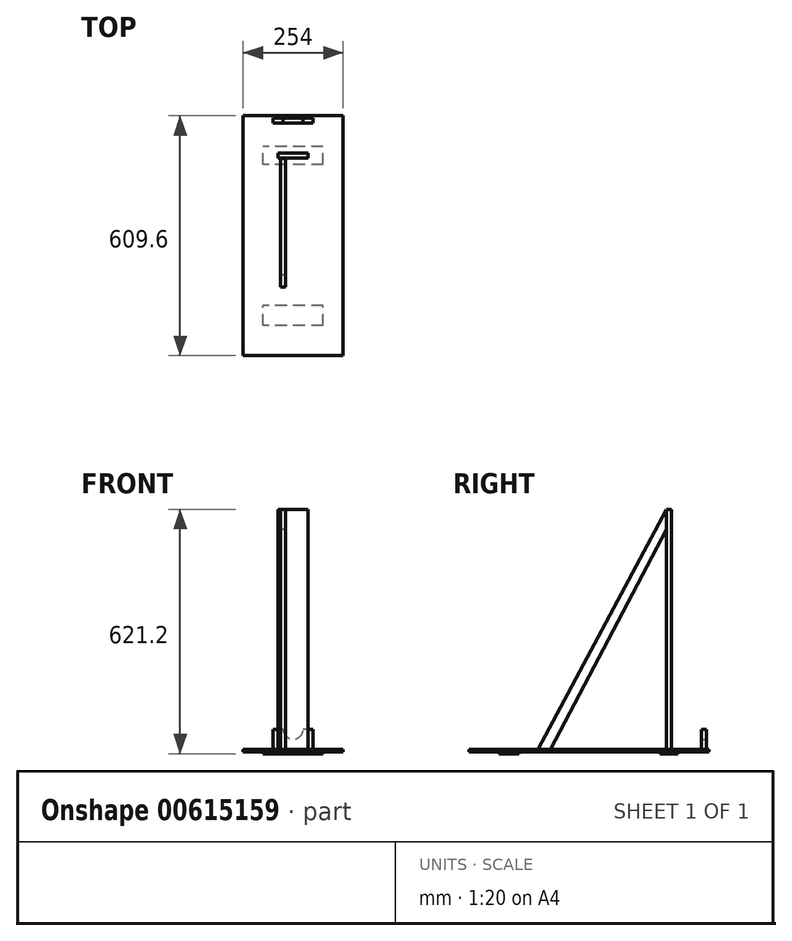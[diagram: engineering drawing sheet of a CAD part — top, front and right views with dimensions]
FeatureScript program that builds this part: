
annotation { "Feature Type Name" : "Feature", "Feature Type Description" : "" }
export const myFeature = defineFeature(function(context is Context, id is Id, definition is map)
    precondition{}
    {
        {
            var Q0;
            Q0=qCreatedBy(makeId("Top.planeOp"),FACE);
            var sketch = newSketch(context, id + "F0", { "sketchPlane" : qUnion([Q0])});
            skLineSegment(sketch, "E0.bottom", {"start": v(152.4, -304.8) * mm, "end": v(-101.6, -304.8) * mm});
            skLineSegment(sketch, "E0.top", {"start": v(152.4, 304.8) * mm, "end": v(-101.6, 304.8) * mm});
            skLineSegment(sketch, "E0.left", {"start": v(152.4, -304.8) * mm, "end": v(152.4, 304.8) * mm});
            skLineSegment(sketch, "E0.right", {"start": v(-101.6, -304.8) * mm, "end": v(-101.6, 304.8) * mm});
            skSolve(sketch);
        }
        {
            var Q0;
            Q0=qSketchRegion(id+"F0",true);
            extrude(context, id + "F1", {"entities" : qUnion([Q0]), "depth" : 6.35 * mm, "offsetDistance" : 25.4 * mm});
        }
        {
            var Q0;
            Q0=makeQuery(id+"F1.opExtrude","CAP_FACE",FACE,{"disambiguationData":[OSD([sQuery(id+"F0.wireOp",EDGE,"E0.bottom"),sQuery(id+"F0.wireOp",EDGE,"E0.top"),sQuery(id+"F0.wireOp",EDGE,"E0.left"),sQuery(id+"F0.wireOp",EDGE,"E0.right")])],"isStart":true});
            var sketch = newSketch(context, id + "F2", { "sketchPlane" : qUnion([Q0])});
            skPoint(sketch, "E1.endSnap0", {"position": v(25.4, 304.8) * mm});
            skLineSegment(sketch, "E2.bottom", {"start": v(101.6, 228.6) * mm, "end": v(-50.8, 228.6) * mm});
            skLineSegment(sketch, "E2.top", {"start": v(101.6, 177.8) * mm, "end": v(-50.8, 177.8) * mm});
            skLineSegment(sketch, "E2.left", {"start": v(101.6, 228.6) * mm, "end": v(101.6, 177.8) * mm});
            skLineSegment(sketch, "E2.right", {"start": v(-50.8, 228.6) * mm, "end": v(-50.8, 177.8) * mm});
            skPoint(sketch, "E2.middle", {"position": v(25.4, 203.2) * mm});
            skLineSegment(sketch, "E3.bottom", {"start": v(101.6, -180.36) * mm, "end": v(-50.8, -180.36) * mm});
            skLineSegment(sketch, "E3.top", {"start": v(101.6, -226.04) * mm, "end": v(-50.8, -226.04) * mm});
            skLineSegment(sketch, "E3.left", {"start": v(101.6, -180.36) * mm, "end": v(101.6, -226.04) * mm});
            skLineSegment(sketch, "E3.right", {"start": v(-50.8, -180.36) * mm, "end": v(-50.8, -226.04) * mm});
            skPoint(sketch, "E3.middle", {"position": v(25.4, -203.2) * mm});
            skSolve(sketch);
        }
        {
            var Q0;
            Q0 = qSketchRegion(id + "F2", true);
            extrude(context, id + "F3", {"entities" : qUnion([Q0]), "operationType" : NewBodyOperationType.ADD, "depth" : 5.08 * mm, "offsetDistance" : 25.4 * mm});
        }
        {
            var Q0;
            Q0=makeQuery(id+"F1.opExtrude","CAP_FACE",FACE,{"disambiguationData":[OSD([sQuery(id+"F0.wireOp",EDGE,"E0.bottom"),sQuery(id+"F0.wireOp",EDGE,"E0.top"),sQuery(id+"F0.wireOp",EDGE,"E0.left"),sQuery(id+"F0.wireOp",EDGE,"E0.right")])],"isStart":false});
            var sketch = newSketch(context, id + "F4", { "sketchPlane" : qUnion([Q0])});
            skLineSegment(sketch, "E4", {"start": v(25.4, 304.8) * mm, "end": v(25.4, 292.1) * mm});
            skLineSegment(sketch, "E5.bottom", {"start": v(76.2, 298.45) * mm, "end": v(-25.4, 298.45) * mm});
            skLineSegment(sketch, "E5.top", {"start": v(76.2, 285.75) * mm, "end": v(-25.4, 285.75) * mm});
            skLineSegment(sketch, "E5.left", {"start": v(76.2, 298.45) * mm, "end": v(76.2, 285.75) * mm});
            skLineSegment(sketch, "E5.right", {"start": v(-25.4, 298.45) * mm, "end": v(-25.4, 285.75) * mm});
            skPoint(sketch, "E5.middle", {"position": v(25.4, 292.1) * mm});
            skSolve(sketch);
        }
        {
            var Q0;
            Q0 = qSketchRegion(id + "F4", true);
            extrude(context, id + "F5", {"entities" : qUnion([Q0]), "operationType" : NewBodyOperationType.ADD, "depth" : 50.8 * mm, "offsetDistance" : 25.4 * mm});
        }
        {
            var Q0;
            Q0=makeQuery(id+"F1.opExtrude","CAP_FACE",FACE,{"disambiguationData":[OSD([sQuery(id+"F0.wireOp",EDGE,"E0.bottom"),sQuery(id+"F0.wireOp",EDGE,"E0.top"),sQuery(id+"F0.wireOp",EDGE,"E0.left"),sQuery(id+"F0.wireOp",EDGE,"E0.right")])],"isStart":false});
            var sketch = newSketch(context, id + "F6", { "sketchPlane" : qUnion([Q0])});
            skPoint(sketch, "E6.endSnap0", {"position": v(25.4, 285.75) * mm});
            skLineSegment(sketch, "E7.bottom", {"start": v(63.5, 209.55) * mm, "end": v(-12.7, 209.55) * mm});
            skLineSegment(sketch, "E7.top", {"start": v(63.5, 196.85) * mm, "end": v(-12.7, 196.85) * mm});
            skLineSegment(sketch, "E7.left", {"start": v(63.5, 209.55) * mm, "end": v(63.5, 196.85) * mm});
            skLineSegment(sketch, "E7.right", {"start": v(-12.7, 209.55) * mm, "end": v(-12.7, 196.85) * mm});
            skPoint(sketch, "E7.middle", {"position": v(25.4, 203.2) * mm});
            skSolve(sketch);
        }
        {
            var Q0;
            Q0 = qSketchRegion(id + "F6", true);
            extrude(context, id + "F7", {"entities" : qUnion([Q0]), "operationType" : NewBodyOperationType.ADD, "depth" : 609.6 * mm, "offsetDistance" : 25.4 * mm});
        }
        {
            var Q0;
            Q0=qCreatedBy(makeId("Right.planeOp"),FACE);
            var sketch = newSketch(context, id + "F8", { "sketchPlane" : qUnion([Q0])});
            skLineSegment(sketch, "E8", {"start": v(0, 0) * mm, "end": v(-203.2, 0) * mm});
            skLineSegment(sketch, "E9", {"start": v(-101.6, 0) * mm, "end": v(196.67, 564.32) * mm});
            skLineSegment(sketch, "E10", {"start": v(196.67, 564.32) * mm, "end": v(196.67, 616.12) * mm});
            skLineSegment(sketch, "E11", {"start": v(196.67, 616.12) * mm, "end": v(-133.41, 0) * mm});
            skLineSegment(sketch, "E12", {"start": v(-133.41, 0) * mm, "end": v(-101.6, 0) * mm});
            skSolve(sketch);
        }
        {
            var Q0;
            Q0 = qSketchRegion(id + "F8", true);
            extrude(context, id + "F9", {"entities" : qUnion([Q0]), "operationType" : NewBodyOperationType.ADD, "depth" : 12.7 * mm, "offsetDistance" : 25.4 * mm, "symmetric" : true});
        }
        {
            var Q0;
            Q0=makeQuery(id+"F5.opExtrude","SWEPT_FACE",FACE,{"disambiguationData":[OSD([sQuery(id+"F4.wireOp",EDGE,"E5.bottom")])]});
            var sketch = newSketch(context, id + "F10", { "sketchPlane" : qUnion([Q0])});
            skArc(sketch, "E13", {"start": v(0, 57.15) * mm, "mid": v(-25.4, 31.75) * mm, "end": v(-50.8, 57.15) * mm});
            skLineSegment(sketch, "E14", {"start": v(-50.8, 57.15) * mm, "end": v(0, 57.15) * mm});
            skSolve(sketch);
        }
        {
            var Q0;
            Q0 = qSketchRegion(id + "F10", true);
            extrude(context, id + "F11", {"entities" : qUnion([Q0]), "operationType" : NewBodyOperationType.REMOVE, "oppositeDirection" : true, "depth" : 25.4 * mm, "offsetDistance" : 25.4 * mm});
        }
    });
